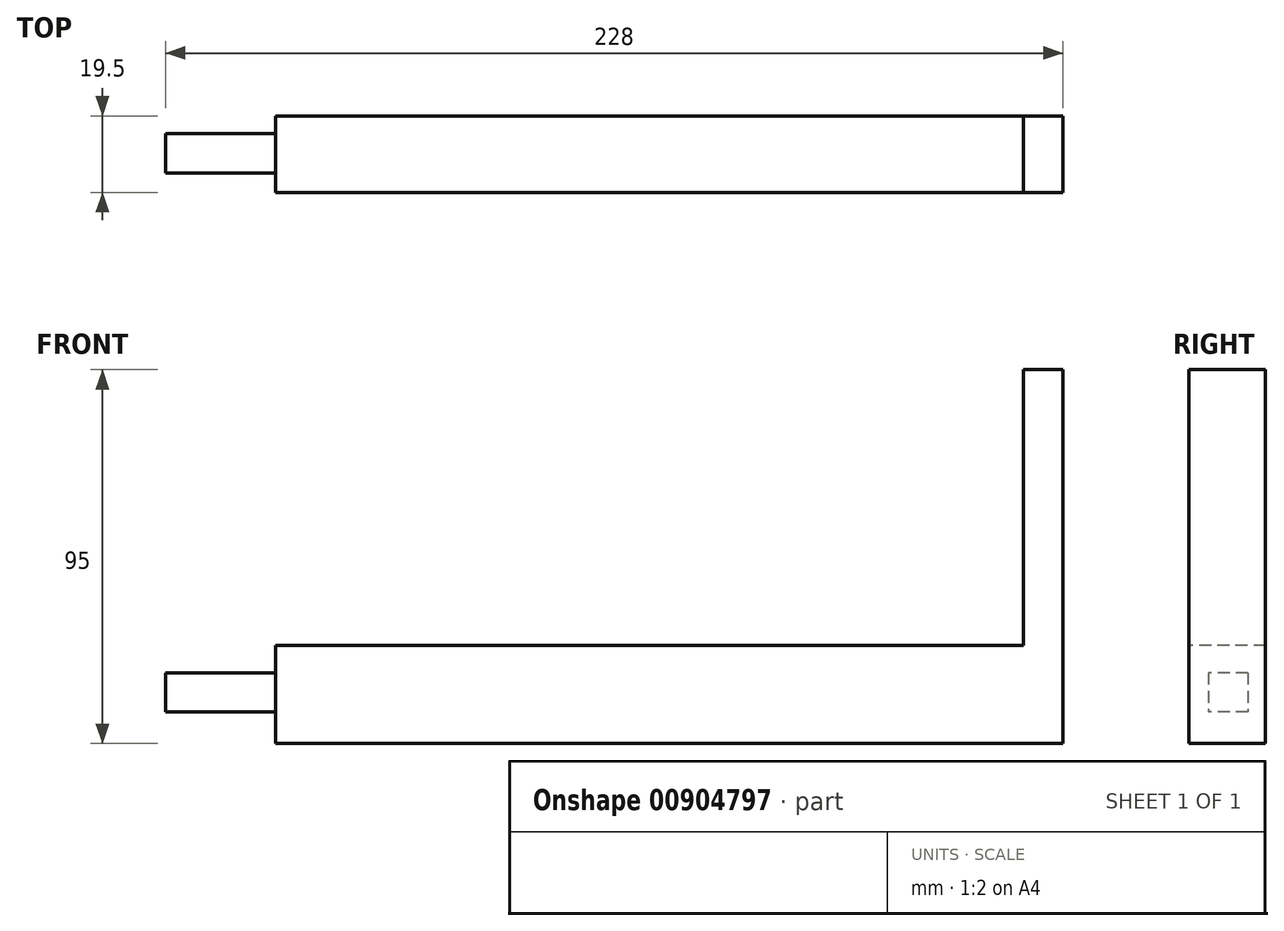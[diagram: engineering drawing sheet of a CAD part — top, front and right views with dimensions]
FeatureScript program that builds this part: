
annotation { "Feature Type Name" : "Feature", "Feature Type Description" : "" }
export const myFeature = defineFeature(function(context is Context, id is Id, definition is map)
    precondition{}
    {
        {
            var Q0;
            Q0=qCreatedBy(makeId("Top.planeOp"),FACE);
            var sketch = newSketch(context, id + "F0", { "sketchPlane" : qUnion([Q0])});
            skLineSegment(sketch, "E0", {"start": v(-68.8, 0.45) * mm, "end": v(131.2, 0.45) * mm});
            skLineSegment(sketch, "E1", {"start": v(131.2, 0.45) * mm, "end": v(131.2, -19.05) * mm});
            skLineSegment(sketch, "E2", {"start": v(131.2, -19.05) * mm, "end": v(-68.8, -19.05) * mm});
            skLineSegment(sketch, "E3", {"start": v(121.2, 0.45) * mm, "end": v(121.2, -19.05) * mm});
            skLineSegment(sketch, "E4", {"start": v(-68.8, 0.45) * mm, "end": v(-68.8, -19.05) * mm});
            skSolve(sketch);
        }
        {
            var Q0;
            {var subQ2=sQuery(id+"F0.wireOp",EDGE,"E3");Q0=makeQuery(id+"F0.imprint","IMPRINT",FACE,{"disambiguationData":[TD([[makeQuery(id+"F0.imprint","IMPRINT",EDGE,{"derivedFrom":subQ2}),-1.0]])]});}
            var Q1;
            {var subQ0=sQuery(id+"F0.wireOp",EDGE,"E1");Q1=makeQuery(id+"F0.imprint","IMPRINT",FACE,{"disambiguationData":[TD([[makeQuery(id+"F0.imprint","IMPRINT",EDGE,{"derivedFrom":subQ0}),-1.0]])]});}
            extrude(context, id + "F1", {"entities" : qUnion([Q0, Q1]), "depth" : 25 * mm, "offsetDistance" : 25 * mm});
        }
        {
            var Q0;
            Q0=makeQuery(id+"F1.opExtrude","CAP_FACE",FACE,{"disambiguationData":[OSD([sQuery(id+"F0.wireOp",EDGE,"E0"),sQuery(id+"F0.wireOp",EDGE,"E1"),sQuery(id+"F0.wireOp",EDGE,"E2"),sQuery(id+"F0.wireOp",EDGE,"E4")])],"isStart":false});
            var sketch = newSketch(context, id + "F2", { "sketchPlane" : qUnion([Q0])});
            skLineSegment(sketch, "E5", {"start": v(121.2, 0.45) * mm, "end": v(121.2, -19.05) * mm});
            skSolve(sketch);
        }
        {
            var Q0;
            {var subQ0=sQuery(id+"F2.wireOp",EDGE,"E5");Q0=makeQuery(id+"F2.imprint","IMPRINT",FACE,{"disambiguationData":[TD([[makeQuery(id+"F2.imprint","IMPRINT",EDGE,{"derivedFrom":subQ0}),1.0]])]});}
            extrude(context, id + "F3", {"entities" : qUnion([Q0]), "operationType" : NewBodyOperationType.ADD, "depth" : 70 * mm, "offsetDistance" : 25 * mm});
        }
        {
            var Q0;
            Q0=makeQuery(id+"F1.opExtrude","SWEPT_FACE",FACE,{"disambiguationData":[OSD([sQuery(id+"F0.wireOp",EDGE,"E4")])]});
            var sketch = newSketch(context, id + "F4", { "sketchPlane" : qUnion([Q0])});
            skLineSegment(sketch, "E6.bottom", {"start": v(4.05, 18) * mm, "end": v(14.05, 18) * mm});
            skLineSegment(sketch, "E6.top", {"start": v(4.05, 8) * mm, "end": v(14.05, 8) * mm});
            skLineSegment(sketch, "E6.left", {"start": v(4.05, 18) * mm, "end": v(4.05, 8) * mm});
            skLineSegment(sketch, "E6.right", {"start": v(14.05, 18) * mm, "end": v(14.05, 8) * mm});
            skSolve(sketch);
        }
        {
            var Q0;
            Q0=makeQuery(id+"F4.imprint","IMPRINT",FACE,{"disambiguationData":[TD([[makeQuery(id+"F4.imprint","IMPRINT",EDGE,{"derivedFrom":sQuery(id+"F4.wireOp",EDGE,"E6.bottom")}),-1.0]])]});
            extrude(context, id + "F5", {"entities" : qUnion([Q0]), "operationType" : NewBodyOperationType.ADD, "depth" : 28 * mm, "offsetDistance" : 25 * mm});
        }
    });
